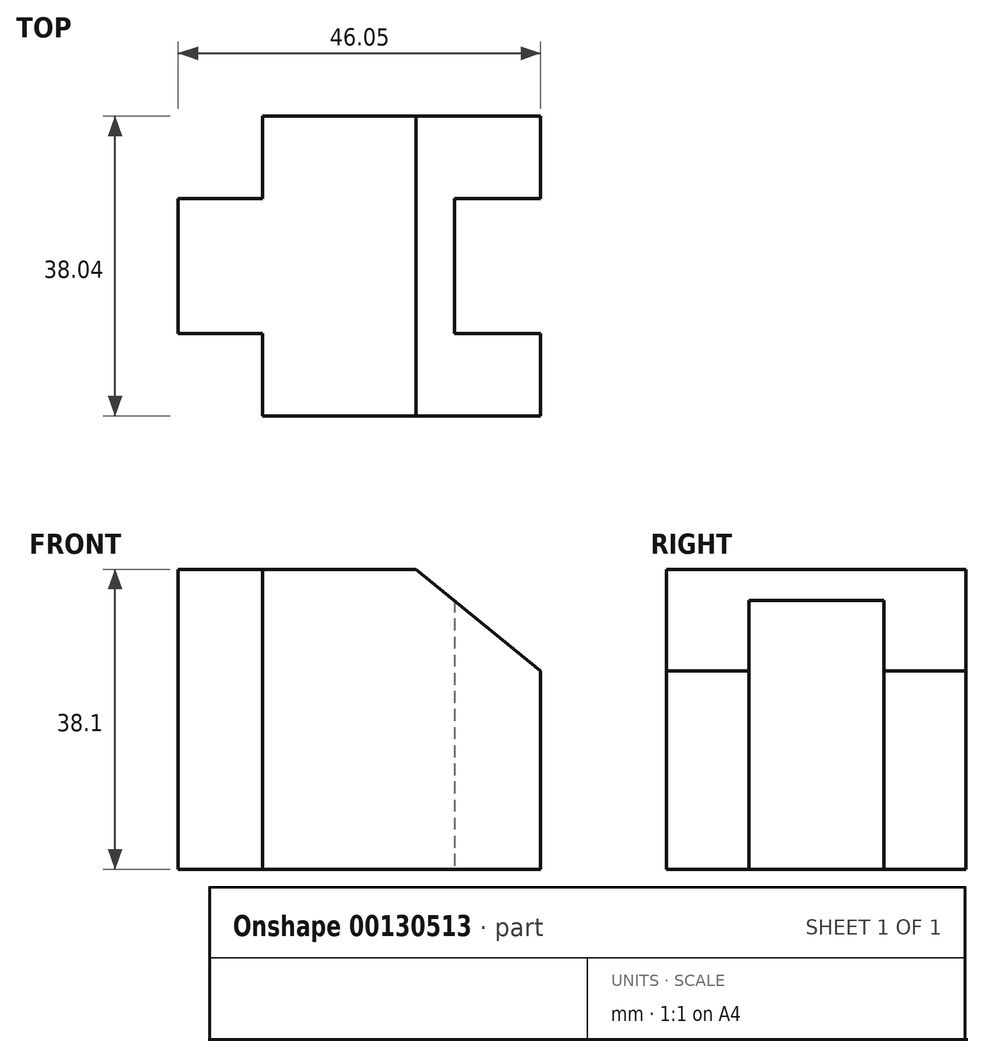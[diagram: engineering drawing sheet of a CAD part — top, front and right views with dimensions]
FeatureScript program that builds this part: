
annotation { "Feature Type Name" : "Feature", "Feature Type Description" : "" }
export const myFeature = defineFeature(function(context is Context, id is Id, definition is map)
    precondition{}
    {
        {
            var Q0;
            Q0=qCreatedBy(makeId("Front.planeOp"),FACE);
            var sketch = newSketch(context, id + "F0", { "sketchPlane" : qUnion([Q0])});
            skLineSegment(sketch, "E0", {"start": v(0, 0) * mm, "end": v(0, 43.04) * mm, "construction": true});
            skLineSegment(sketch, "E1", {"start": v(0, 43.04) * mm, "end": v(10.74, 43.04) * mm, "construction": true});
            skLineSegment(sketch, "E2", {"start": v(10.74, 43.04) * mm, "end": v(10.74, 0) * mm, "construction": true});
            skLineSegment(sketch, "E3", {"start": v(10.74, 0) * mm, "end": v(0, 0) * mm});
            skLineSegment(sketch, "E4", {"start": v(10.74, 0) * mm, "end": v(46.05, 0) * mm, "construction": true});
            skLineSegment(sketch, "E5", {"start": v(46.05, 0) * mm, "end": v(46.05, 25.22) * mm, "construction": true});
            skLineSegment(sketch, "E6", {"start": v(46.05, 25.22) * mm, "end": v(24.1, 43.04) * mm});
            skLineSegment(sketch, "E7", {"start": v(24.1, 43.04) * mm, "end": v(10.74, 43.04) * mm, "construction": true});
            skLineSegment(sketch, "E8", {"start": v(35.08, 34.13) * mm, "end": v(35.08, 0) * mm, "construction": true});
            skLineSegment(sketch, "E9", {"start": v(24.1, 43.04) * mm, "end": v(46.05, 43.04) * mm});
            skLineSegment(sketch, "E10", {"start": v(46.05, 43.04) * mm, "end": v(46.05, 25.22) * mm});
            skSolve(sketch);
        }
        {
            var Q0;
            Q0=qCreatedBy(makeId("Top.planeOp"),FACE);
            var sketch = newSketch(context, id + "F1", { "sketchPlane" : qUnion([Q0])});
            skLineSegment(sketch, "E11", {"start": v(46.05, 0) * mm, "end": v(10.74, 0) * mm});
            skLineSegment(sketch, "E12", {"start": v(10.74, 0) * mm, "end": v(10.74, 10.44) * mm});
            skLineSegment(sketch, "E13", {"start": v(10.74, 10.44) * mm, "end": v(0, 10.44) * mm});
            skLineSegment(sketch, "E14", {"start": v(0, 10.44) * mm, "end": v(0, 27.6) * mm});
            skLineSegment(sketch, "E15", {"start": v(0, 27.6) * mm, "end": v(10.74, 27.6) * mm});
            skLineSegment(sketch, "E16", {"start": v(10.74, 27.6) * mm, "end": v(10.74, 38.04) * mm});
            skLineSegment(sketch, "E17", {"start": v(10.74, 38.04) * mm, "end": v(46.05, 38.04) * mm});
            skLineSegment(sketch, "E18", {"start": v(46.05, 38.04) * mm, "end": v(46.05, 27.6) * mm});
            skLineSegment(sketch, "E19", {"start": v(46.05, 27.6) * mm, "end": v(35.08, 27.6) * mm});
            skLineSegment(sketch, "E20", {"start": v(35.08, 27.6) * mm, "end": v(35.08, 10.44) * mm});
            skLineSegment(sketch, "E21", {"start": v(35.08, 10.44) * mm, "end": v(46.05, 10.44) * mm});
            skLineSegment(sketch, "E22", {"start": v(46.05, 10.44) * mm, "end": v(46.05, 0) * mm});
            skLineSegment(sketch, "E23", {"start": v(24.1, 0) * mm, "end": v(24.1, 38.04) * mm});
            skSolve(sketch);
        }
        {
            var Q0;
            Q0 = qSketchRegion(id + "F1", true);
            extrude(context, id + "F2", {"entities" : qUnion([Q0]), "depth" : 38.1 * mm});
        }
        {
            var Q0;
            Q0 = qSketchRegion(id + "F0", true);
            extrude(context, id + "F3", {"entities" : qUnion([Q0]), "operationType" : NewBodyOperationType.REMOVE, "oppositeDirection" : true, "depth" : 50.8 * mm});
        }
    });
